# Revit family: VRO-ACPMK
name_source: partatom
category: Lighting Fixtures
units: mm (PartAtom-declared; Revit-internal decimal feet)

## family parameters
Cut with Voids When Loaded = Yes
Host = Face
Light Source = Yes
Maintain Annotation Orientation = No
Part Type = Normal
Room Calculation Point = No
Round Connector Dimension = Use Diameter
Shared = No

## types (4) — shared parameters
A = 0' - 10"
Beam Angle = 0.00°
CRI = 90
Color Filter = 16777215
Default Elevation = 0' - 0"
Dimming Lamp Color Temperature Shift = <None>
Input Voltage = 120-277V
Lamp = LED
Load Classification = Lighting
Manufacturer = Above All Lighting
Note = The actual cable count varies with the fixture size.
Power Factor = 0.9
Suspension = 3' - 0"
Tilt Angle = 90.00°

## per-type parameters (varying)
| type | Model | Photometric Web File | R | Wattage Comments | cable |
| VRO-32W-4000K-ACPMK | VRO-3624-40901-ACPMK-WH | VRO_3624_40901_WH.ies | 0' - 11 13/16" | 32W | 0' - 11 25/32" |
| VRO-40W-3000K-ACPMK | VRO-4035-30901-ACPMK-WH | VRO_4035_30901_WH.ies | 1' - 5 11/16" | 40W | 1' - 5 21/32" |
| VRO-70W-3000K-ACPMK | VRO-7047-30901-ACPMK-WH | VRO_7047_30901_WH.ies | 1' - 11 19/32" | 70W | 1' - 11 9/16" |
| VRO-80W-3000K-ACPMK | VRO-8059-30901-ACPMK-WH | VRO_8059_30901_WH.ies | 2' - 5 9/16" | 80W | 2' - 5 17/32" |

## geometry (parser evidence)
native form markers: Sweep x2
no freeform markers — native parametric forms only
